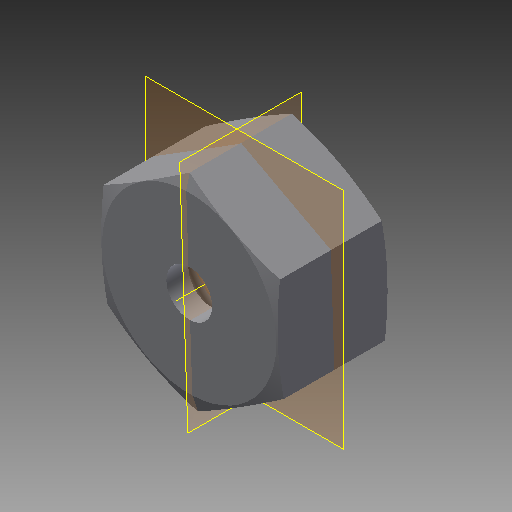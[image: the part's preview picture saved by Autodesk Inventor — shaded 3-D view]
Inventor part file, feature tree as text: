
AUTODESK INVENTOR PART (.ipt)
format: ipt  version: 2017 (Build 210142000, 142)  size: 143,360 bytes
history: native  units: in
note: dims shown in document units (in); Inventor stores cm internally (conversion verified against a paired STEP export)
features: sketch x4, plane x3, extrude x3, reference x2, thread x1, other x1, revolve x1, mirror x1
ambient origin geometry x8: Origin, YZ Plane, XZ Plane, XY Plane, X Axis, Y Axis, Z Axis, Center Point
bodies: Body1 (feature_tree)
feature tree (16):
  plane  "Work Plane3"
  extrude  "Extrusion2"  Depth=0.5in
  extrude  "Extrusion3"  Depth=0.375in TaperAngle=0.0deg
  extrude  "Extrusion4"  TaperAngle=90.0deg  [1 undecoded]
  thread  "Thread1"  [1 undecoded]
  plane  "Work Plane4"
  other  "Work Axis4"
  revolve  "Revolution2"  [1 undecoded]
  plane  "Work Plane5"
  mirror  "Mirror1"
  sketch  "Sketch6"  dims[d3=0.3125in d4=0.0in d5=0.5in]
  sketch  "Sketch7"  dims[d6=0.25in d7=-0.0123in d8=0.375in d9=0.0in]
  reference  "Reference1"
  sketch  "Sketch8"  dims[d10=0.392in d11=0.0in d12=90.0deg d13=0.045in]
  reference  "Reference2"
  sketch  "Sketch9"
note: 3 required parameter values undecoded (feature->parameter linkage not recoverable at this tier; creation-order binding heuristic only, values carry confidence <= 0.55)
